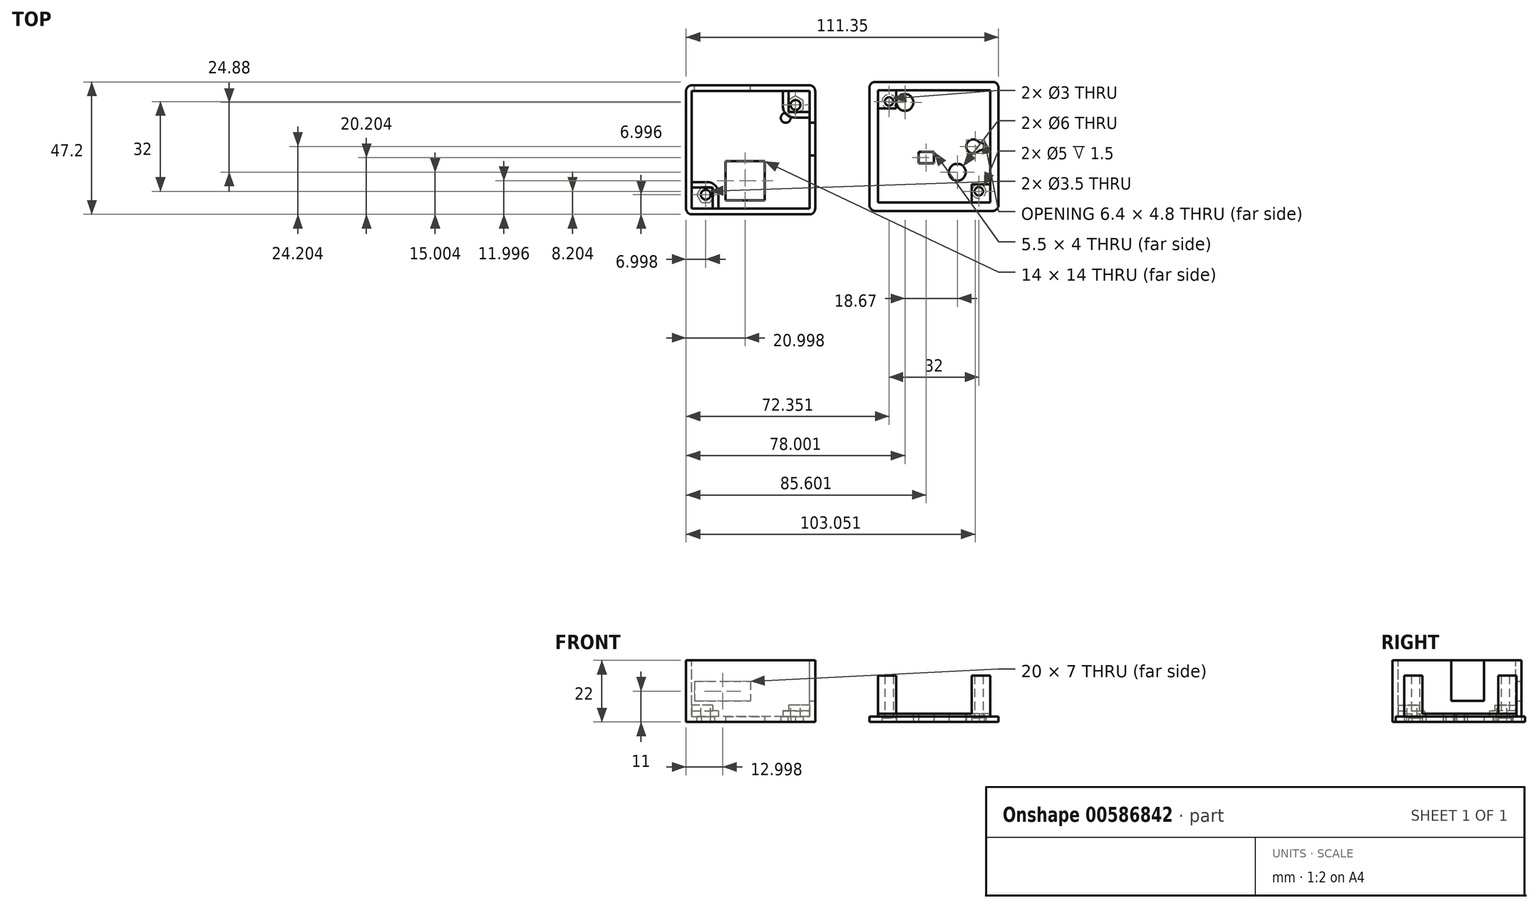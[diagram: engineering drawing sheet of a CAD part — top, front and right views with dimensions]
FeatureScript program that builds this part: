
annotation { "Feature Type Name" : "Feature", "Feature Type Description" : "" }
export const myFeature = defineFeature(function(context is Context, id is Id, definition is map)
    precondition{}
    {
        {
            var Q0;
            Q0=qCreatedBy(makeId("Top.planeOp"),FACE);
            var sketch = newSketch(context, id + "F0", { "sketchPlane" : qUnion([Q0])});
            skLineSegment(sketch, "E0.bottom", {"start": v(-57.81, 60.95) * mm, "end": v(-11.81, 60.95) * mm});
            skLineSegment(sketch, "E0.top", {"start": v(-57.81, 14.95) * mm, "end": v(-11.81, 14.95) * mm});
            skLineSegment(sketch, "E0.left", {"start": v(-57.81, 60.95) * mm, "end": v(-57.81, 14.95) * mm});
            skLineSegment(sketch, "E0.right", {"start": v(-11.81, 60.95) * mm, "end": v(-11.81, 14.95) * mm});
            skSolve(sketch);
        }
        {
            var Q0;
            Q0=makeQuery(id+"F0.imprint","IMPRINT",FACE,{"disambiguationData":[TD([[makeQuery(id+"F0.imprint","IMPRINT",EDGE,{"derivedFrom":sQuery(id+"F0.wireOp",EDGE,"E0.bottom")}),-1.0]])]});
            extrude(context, id + "F1", {"entities" : qUnion([Q0]), "depth" : 22 * mm, "offsetDistance" : 25 * mm});
        }
        {
            var Q0;
            Q0=makeQuery(id+"F1.opExtrude","CAP_FACE",FACE,{"disambiguationData":[OSD([sQuery(id+"F0.wireOp",EDGE,"E0.bottom"),sQuery(id+"F0.wireOp",EDGE,"E0.top"),sQuery(id+"F0.wireOp",EDGE,"E0.left"),sQuery(id+"F0.wireOp",EDGE,"E0.right")])],"isStart":false});
            var sketch = newSketch(context, id + "F2", { "sketchPlane" : qUnion([Q0])});
            skLineSegment(sketch, "E1.bottom", {"start": v(-13.81, 16.95) * mm, "end": v(-55.81, 16.95) * mm});
            skLineSegment(sketch, "E1.top", {"start": v(-13.81, 58.95) * mm, "end": v(-55.81, 58.95) * mm});
            skLineSegment(sketch, "E1.left", {"start": v(-13.81, 16.95) * mm, "end": v(-13.81, 58.95) * mm});
            skLineSegment(sketch, "E1.right", {"start": v(-55.81, 16.95) * mm, "end": v(-55.81, 58.95) * mm});
            skPoint(sketch, "E1.middle", {"position": v(-34.81, 37.95) * mm});
            skPoint(sketch, "E1.middle.positionSnap0", {"position": v(-57.81, 37.95) * mm});
            skPoint(sketch, "E1.middle.positionSnap1", {"position": v(-34.81, 60.95) * mm});
            skPoint(sketch, "E1.centerSnap0", {"position": v(-57.81, 37.95) * mm});
            skPoint(sketch, "E1.centerSnap1", {"position": v(-34.81, 60.95) * mm});
            skSolve(sketch);
        }
        {
            var Q0;
            Q0=makeQuery(id+"F2.imprint","IMPRINT",FACE,{"disambiguationData":[TD([[makeQuery(id+"F2.imprint","IMPRINT",EDGE,{"derivedFrom":sQuery(id+"F2.wireOp",EDGE,"E1.bottom")}),-1.0]])]});
            extrude(context, id + "F3", {"entities" : qUnion([Q0]), "operationType" : NewBodyOperationType.REMOVE, "oppositeDirection" : true, "depth" : 20 * mm, "offsetDistance" : 25 * mm});
        }
        {
            var Q0;
            Q0=makeQuery(id+"F3.boolean.opBoolean","COPY",FACE,{"derivedFrom":makeQuery(id+"F3.opExtrude","CAP_FACE",FACE,{"disambiguationData":[OSD([sQuery(id+"F2.wireOp",EDGE,"E1.bottom"),sQuery(id+"F2.wireOp",EDGE,"E1.top"),sQuery(id+"F2.wireOp",EDGE,"E1.left"),sQuery(id+"F2.wireOp",EDGE,"E1.right")])],"isStart":false})});
            var sketch = newSketch(context, id + "F4", { "sketchPlane" : qUnion([Q0])});
            skLineSegment(sketch, "E2.bottom", {"start": v(-55.81, 16.95) * mm, "end": v(-48.31, 16.95) * mm});
            skLineSegment(sketch, "E2.top", {"start": v(-55.81, 24.45) * mm, "end": v(-48.31, 24.45) * mm});
            skLineSegment(sketch, "E2.left", {"start": v(-55.81, 16.95) * mm, "end": v(-55.81, 24.45) * mm});
            skLineSegment(sketch, "E2.right", {"start": v(-48.31, 16.95) * mm, "end": v(-48.31, 24.45) * mm});
            skLineSegment(sketch, "E3.bottom", {"start": v(-13.81, 58.95) * mm, "end": v(-21.31, 58.95) * mm});
            skLineSegment(sketch, "E3.top", {"start": v(-13.81, 51.45) * mm, "end": v(-21.31, 51.45) * mm});
            skLineSegment(sketch, "E3.left", {"start": v(-13.81, 58.95) * mm, "end": v(-13.81, 51.45) * mm});
            skLineSegment(sketch, "E3.right", {"start": v(-21.31, 58.95) * mm, "end": v(-21.31, 51.45) * mm});
            skSolve(sketch);
        }
        {
            var Q0;
            Q0 = qSketchRegion(id + "F4", true);
            extrude(context, id + "F5", {"entities" : qUnion([Q0]), "operationType" : NewBodyOperationType.ADD, "depth" : 4 * mm, "offsetDistance" : 25 * mm});
        }
        {
            var Q0;
            Q0=makeQuery(id+"F5.boolean.opBoolean","MERGE",FACE,{"derivedFrom":[makeQuery(id+"F1.opExtrude","CAP_FACE",FACE,{"disambiguationData":[OSD([sQuery(id+"F0.wireOp",EDGE,"E0.bottom"),sQuery(id+"F0.wireOp",EDGE,"E0.top"),sQuery(id+"F0.wireOp",EDGE,"E0.left"),sQuery(id+"F0.wireOp",EDGE,"E0.right")])],"isStart":false}),makeQuery(id+"F5.opExtrude","CAP_FACE",FACE,{"disambiguationData":[OSD([sQuery(id+"F4.wireOp",EDGE,"E2.bottom"),sQuery(id+"F4.wireOp",EDGE,"E2.top"),sQuery(id+"F4.wireOp",EDGE,"E2.left"),sQuery(id+"F4.wireOp",EDGE,"E2.right")])],"isStart":false}),makeQuery(id+"F5.opExtrude","CAP_FACE",FACE,{"disambiguationData":[OSD([sQuery(id+"F4.wireOp",EDGE,"LOzcj4NV-yvEm-kmDy-pfsw-HTMoK0iiiUwV.bottom"),sQuery(id+"F4.wireOp",EDGE,"LOzcj4NV-yvEm-kmDy-pfsw-HTMoK0iiiUwV.top"),sQuery(id+"F4.wireOp",EDGE,"LOzcj4NV-yvEm-kmDy-pfsw-HTMoK0iiiUwV.left"),sQuery(id+"F4.wireOp",EDGE,"LOzcj4NV-yvEm-kmDy-pfsw-HTMoK0iiiUwV.right")])],"isStart":false}),makeQuery(id+"F5.opExtrude","CAP_FACE",FACE,{"disambiguationData":[OSD([sQuery(id+"F4.wireOp",EDGE,"E3.bottom"),sQuery(id+"F4.wireOp",EDGE,"E3.top"),sQuery(id+"F4.wireOp",EDGE,"E3.left"),sQuery(id+"F4.wireOp",EDGE,"E3.right")])],"isStart":false}),makeQuery(id+"F5.opExtrude","CAP_FACE",FACE,{"disambiguationData":[OSD([sQuery(id+"F4.wireOp",EDGE,"QqbcK2UQ-hBf6-F2q0-HRpz-6xSYQiyMGXhG.bottom"),sQuery(id+"F4.wireOp",EDGE,"QqbcK2UQ-hBf6-F2q0-HRpz-6xSYQiyMGXhG.top"),sQuery(id+"F4.wireOp",EDGE,"QqbcK2UQ-hBf6-F2q0-HRpz-6xSYQiyMGXhG.left"),sQuery(id+"F4.wireOp",EDGE,"QqbcK2UQ-hBf6-F2q0-HRpz-6xSYQiyMGXhG.right")])],"isStart":false})]});
            var sketch = newSketch(context, id + "F6", { "sketchPlane" : qUnion([Q0])});
            skCircle(sketch, "E4", {"center": v(-18.81, 53.95) * mm, "radius": 1.75 * mm});
            skCircle(sketch, "E5", {"center": v(-50.81, 21.95) * mm, "radius": 1.75 * mm});
            skSolve(sketch);
        }
        {
            var Q0;
            Q0=makeQuery(id+"F3.boolean.opBoolean","COPY",FACE,{"derivedFrom":makeQuery(id+"F3.opExtrude","CAP_FACE",FACE,{"disambiguationData":[OSD([sQuery(id+"F2.wireOp",EDGE,"E1.bottom"),sQuery(id+"F2.wireOp",EDGE,"E1.top"),sQuery(id+"F2.wireOp",EDGE,"E1.left"),sQuery(id+"F2.wireOp",EDGE,"E1.right")])],"isStart":false})});
            var sketch = newSketch(context, id + "F7", { "sketchPlane" : qUnion([Q0])});
            skLineSegment(sketch, "E6.bottom", {"start": v(-21.31, 58.95) * mm, "end": v(-23.31, 58.95) * mm});
            skLineSegment(sketch, "E6.top", {"start": v(-21.31, 51.45) * mm, "end": v(-23.31, 51.45) * mm});
            skLineSegment(sketch, "E6.left", {"start": v(-21.31, 58.95) * mm, "end": v(-21.31, 51.45) * mm});
            skLineSegment(sketch, "E6.right", {"start": v(-23.31, 58.95) * mm, "end": v(-23.31, 51.45) * mm});
            skLineSegment(sketch, "E7.bottom", {"start": v(-23.31, 51.45) * mm, "end": v(-13.81, 51.45) * mm});
            skLineSegment(sketch, "E7.top", {"start": v(-23.31, 49.45) * mm, "end": v(-13.81, 49.45) * mm});
            skLineSegment(sketch, "E7.left", {"start": v(-23.31, 51.45) * mm, "end": v(-23.31, 49.45) * mm});
            skLineSegment(sketch, "E7.right", {"start": v(-13.81, 51.45) * mm, "end": v(-13.81, 49.45) * mm});
            skLineSegment(sketch, "E8.bottom", {"start": v(-55.81, 24.45) * mm, "end": v(-46.31, 24.45) * mm});
            skLineSegment(sketch, "E8.top", {"start": v(-55.81, 26.45) * mm, "end": v(-46.31, 26.45) * mm});
            skLineSegment(sketch, "E8.left", {"start": v(-55.81, 24.45) * mm, "end": v(-55.81, 26.45) * mm});
            skLineSegment(sketch, "E8.right", {"start": v(-46.31, 24.45) * mm, "end": v(-46.31, 26.45) * mm});
            skLineSegment(sketch, "E9.bottom", {"start": v(-48.31, 16.95) * mm, "end": v(-46.31, 16.95) * mm});
            skLineSegment(sketch, "E9.top", {"start": v(-48.31, 24.45) * mm, "end": v(-46.31, 24.45) * mm});
            skLineSegment(sketch, "E9.left", {"start": v(-48.31, 16.95) * mm, "end": v(-48.31, 24.45) * mm});
            skLineSegment(sketch, "E9.right", {"start": v(-46.31, 16.95) * mm, "end": v(-46.31, 24.45) * mm});
            skSolve(sketch);
        }
        {
            var Q0;
            Q0=makeQuery(id+"F7.imprint","IMPRINT",FACE,{"disambiguationData":[TD([[makeQuery(id+"F7.imprint","IMPRINT",EDGE,{"derivedFrom":sQuery(id+"F7.wireOp",EDGE,"E8.bottom")}),1.0]])]});
            var Q1;
            Q1=makeQuery(id+"F7.imprint","IMPRINT",FACE,{"disambiguationData":[TD([[makeQuery(id+"F7.imprint","IMPRINT",EDGE,{"derivedFrom":sQuery(id+"F7.wireOp",EDGE,"E9.bottom")}),-1.0]])]});
            var Q2;
            Q2=makeQuery(id+"F7.imprint","IMPRINT",FACE,{"disambiguationData":[TD([[makeQuery(id+"F7.imprint","IMPRINT",EDGE,{"derivedFrom":sQuery(id+"F7.wireOp",EDGE,"E6.bottom")}),1.0]])]});
            var Q3;
            Q3=makeQuery(id+"F7.imprint","IMPRINT",FACE,{"disambiguationData":[TD([[makeQuery(id+"F7.imprint","IMPRINT",EDGE,{"derivedFrom":sQuery(id+"F7.wireOp",EDGE,"E7.top")}),1.0]])]});
            extrude(context, id + "F8", {"entities" : qUnion([Q0, Q1, Q2, Q3]), "operationType" : NewBodyOperationType.ADD, "depth" : 2 * mm, "offsetDistance" : 25 * mm});
        }
        {
            var Q0;
            Q0=makeQuery(id+"F1.opExtrude","CAP_FACE",FACE,{"disambiguationData":[OSD([sQuery(id+"F0.wireOp",EDGE,"E0.bottom"),sQuery(id+"F0.wireOp",EDGE,"E0.top"),sQuery(id+"F0.wireOp",EDGE,"E0.left"),sQuery(id+"F0.wireOp",EDGE,"E0.right")])],"isStart":true});
            var sketch = newSketch(context, id + "F9", { "sketchPlane" : qUnion([Q0])});
            skCircle(sketch, "E10.cCircle", {"center": v(-18.81, -53.95) * mm, "radius": 2.75 * mm, "construction": true});
            skLineSegment(sketch, "E10.0", {"start": v(-16.06, -52.36) * mm, "end": v(-16.06, -55.53) * mm});
            skLineSegment(sketch, "E10.1", {"start": v(-16.06, -55.53) * mm, "end": v(-18.81, -57.12) * mm});
            skLineSegment(sketch, "E10.2", {"start": v(-18.81, -57.12) * mm, "end": v(-21.56, -55.53) * mm});
            skLineSegment(sketch, "E10.3", {"start": v(-21.56, -55.53) * mm, "end": v(-21.56, -52.36) * mm});
            skLineSegment(sketch, "E10.4", {"start": v(-21.56, -52.36) * mm, "end": v(-18.81, -50.77) * mm});
            skLineSegment(sketch, "E10.5", {"start": v(-18.81, -50.77) * mm, "end": v(-16.06, -52.36) * mm});
            skPoint(sketch, "E10.0.midPoint", {"position": v(-16.06, -53.95) * mm});
            skCircle(sketch, "E11.cCircle", {"center": v(-50.81, -21.95) * mm, "radius": 2.75 * mm, "construction": true});
            skLineSegment(sketch, "E11.0", {"start": v(-49.22, -19.2) * mm, "end": v(-47.64, -21.95) * mm});
            skLineSegment(sketch, "E11.1", {"start": v(-47.64, -21.95) * mm, "end": v(-49.22, -24.7) * mm});
            skLineSegment(sketch, "E11.2", {"start": v(-49.22, -24.7) * mm, "end": v(-52.4, -24.7) * mm});
            skLineSegment(sketch, "E11.3", {"start": v(-52.4, -24.7) * mm, "end": v(-53.99, -21.95) * mm});
            skLineSegment(sketch, "E11.4", {"start": v(-53.99, -21.95) * mm, "end": v(-52.4, -19.2) * mm});
            skLineSegment(sketch, "E11.5", {"start": v(-52.4, -19.2) * mm, "end": v(-49.22, -19.2) * mm});
            skPoint(sketch, "E11.0.midPoint", {"position": v(-48.43, -20.57) * mm});
            skSolve(sketch);
        }
        {
            var Q0;
            Q0=makeQuery(id+"F9.imprint","IMPRINT",FACE,{"disambiguationData":[TD([[makeQuery(id+"F9.imprint","IMPRINT",EDGE,{"derivedFrom":sQuery(id+"F9.wireOp",EDGE,"E10.0")}),-1.0]])]});
            var Q1;
            Q1=makeQuery(id+"F9.imprint","IMPRINT",FACE,{"disambiguationData":[TD([[makeQuery(id+"F9.imprint","IMPRINT",EDGE,{"derivedFrom":sQuery(id+"F9.wireOp",EDGE,"E11.0")}),-1.0]])]});
            extrude(context, id + "F10", {"entities" : qUnion([Q0, Q1]), "operationType" : NewBodyOperationType.REMOVE, "oppositeDirection" : true, "depth" : 2 * mm, "offsetDistance" : 25 * mm});
        }
        {
            var Q0;
            Q0=qCreatedBy(makeId("Top.planeOp"),FACE);
            var sketch = newSketch(context, id + "F11", { "sketchPlane" : qUnion([Q0])});
            skLineSegment(sketch, "E12.bottom", {"start": v(7.54, 62.15) * mm, "end": v(53.54, 62.15) * mm});
            skLineSegment(sketch, "E12.top", {"start": v(7.54, 16.15) * mm, "end": v(53.54, 16.15) * mm});
            skLineSegment(sketch, "E12.left", {"start": v(7.54, 62.15) * mm, "end": v(7.54, 16.15) * mm});
            skLineSegment(sketch, "E12.right", {"start": v(53.54, 62.15) * mm, "end": v(53.54, 16.15) * mm});
            skSolve(sketch);
        }
        {
            var Q0;
            Q0=makeQuery(id+"F11.imprint","IMPRINT",FACE,{"disambiguationData":[TD([[makeQuery(id+"F11.imprint","IMPRINT",EDGE,{"derivedFrom":sQuery(id+"F11.wireOp",EDGE,"E12.bottom")}),-1.0]])]});
            extrude(context, id + "F12", {"entities" : qUnion([Q0]), "depth" : 2 * mm, "offsetDistance" : 25 * mm});
        }
        {
            var Q0;
            Q0=makeQuery(id+"F12.opExtrude","CAP_FACE",FACE,{"disambiguationData":[OSD([sQuery(id+"F11.wireOp",EDGE,"E12.bottom"),sQuery(id+"F11.wireOp",EDGE,"E12.top"),sQuery(id+"F11.wireOp",EDGE,"E12.left"),sQuery(id+"F11.wireOp",EDGE,"E12.right")])],"isStart":false});
            var sketch = newSketch(context, id + "F13", { "sketchPlane" : qUnion([Q0])});
            skLineSegment(sketch, "E13.bottom", {"start": v(50.54, 19.15) * mm, "end": v(10.54, 19.15) * mm});
            skLineSegment(sketch, "E13.top", {"start": v(50.54, 59.15) * mm, "end": v(10.54, 59.15) * mm});
            skLineSegment(sketch, "E13.left", {"start": v(50.54, 19.15) * mm, "end": v(50.54, 59.15) * mm});
            skLineSegment(sketch, "E13.right", {"start": v(10.54, 19.15) * mm, "end": v(10.54, 59.15) * mm});
            skPoint(sketch, "E13.middle", {"position": v(30.54, 39.15) * mm});
            skPoint(sketch, "E13.middle.positionSnap0", {"position": v(7.54, 39.15) * mm});
            skPoint(sketch, "E13.middle.positionSnap1", {"position": v(30.54, 62.15) * mm});
            skPoint(sketch, "E13.centerSnap0", {"position": v(7.54, 39.15) * mm});
            skPoint(sketch, "E13.centerSnap1", {"position": v(30.54, 62.15) * mm});
            skSolve(sketch);
        }
        {
            var Q0;
            Q0=makeQuery(id+"F13.imprint","IMPRINT",FACE,{"disambiguationData":[TD([[makeQuery(id+"F13.imprint","IMPRINT",EDGE,{"derivedFrom":sQuery(id+"F13.wireOp",EDGE,"E13.bottom")}),-1.0]])]});
            extrude(context, id + "F14", {"entities" : qUnion([Q0]), "operationType" : NewBodyOperationType.ADD, "depth" : 1 * mm, "offsetDistance" : 25 * mm});
        }
        {
            var Q0;
            Q0=makeQuery(id+"F14.opExtrude","CAP_FACE",FACE,{"disambiguationData":[OSD([sQuery(id+"F13.wireOp",EDGE,"E13.bottom"),sQuery(id+"F13.wireOp",EDGE,"E13.top"),sQuery(id+"F13.wireOp",EDGE,"E13.left"),sQuery(id+"F13.wireOp",EDGE,"E13.right")])],"isStart":false});
            var sketch = newSketch(context, id + "F15", { "sketchPlane" : qUnion([Q0])});
            skLineSegment(sketch, "E14.bottom", {"start": v(10.54, 59.15) * mm, "end": v(17.04, 59.15) * mm});
            skLineSegment(sketch, "E14.top", {"start": v(10.54, 52.65) * mm, "end": v(17.04, 52.65) * mm});
            skLineSegment(sketch, "E14.left", {"start": v(10.54, 59.15) * mm, "end": v(10.54, 52.65) * mm});
            skLineSegment(sketch, "E14.right", {"start": v(17.04, 59.15) * mm, "end": v(17.04, 52.65) * mm});
            skLineSegment(sketch, "E15.bottom", {"start": v(10.54, 19.15) * mm, "end": v(17.04, 19.15) * mm});
            skLineSegment(sketch, "E15.top", {"start": v(10.54, 25.65) * mm, "end": v(17.04, 25.65) * mm});
            skLineSegment(sketch, "E15.left", {"start": v(10.54, 19.15) * mm, "end": v(10.54, 25.65) * mm});
            skLineSegment(sketch, "E15.right", {"start": v(17.04, 19.15) * mm, "end": v(17.04, 25.65) * mm});
            skLineSegment(sketch, "E16.bottom", {"start": v(50.54, 19.15) * mm, "end": v(44.04, 19.15) * mm});
            skLineSegment(sketch, "E16.top", {"start": v(50.54, 25.65) * mm, "end": v(44.04, 25.65) * mm});
            skLineSegment(sketch, "E16.left", {"start": v(50.54, 19.15) * mm, "end": v(50.54, 25.65) * mm});
            skLineSegment(sketch, "E16.right", {"start": v(44.04, 19.15) * mm, "end": v(44.04, 25.65) * mm});
            skLineSegment(sketch, "E17.bottom", {"start": v(50.54, 59.15) * mm, "end": v(44.04, 59.15) * mm});
            skLineSegment(sketch, "E17.top", {"start": v(50.54, 52.65) * mm, "end": v(44.04, 52.65) * mm});
            skLineSegment(sketch, "E17.left", {"start": v(50.54, 59.15) * mm, "end": v(50.54, 52.65) * mm});
            skLineSegment(sketch, "E17.right", {"start": v(44.04, 59.15) * mm, "end": v(44.04, 52.65) * mm});
            skSolve(sketch);
        }
        {
            var Q0;
            Q0=makeQuery(id+"F15.imprint","IMPRINT",FACE,{"disambiguationData":[TD([[makeQuery(id+"F15.imprint","IMPRINT",EDGE,{"derivedFrom":sQuery(id+"F15.wireOp",EDGE,"E14.bottom")}),1.0]])]});
            var Q1;
            Q1=makeQuery(id+"F15.imprint","IMPRINT",FACE,{"disambiguationData":[TD([[makeQuery(id+"F15.imprint","IMPRINT",EDGE,{"derivedFrom":sQuery(id+"F15.wireOp",EDGE,"E16.bottom")}),-1.0]])]});
            extrude(context, id + "F16", {"entities" : qUnion([Q0, Q1]), "operationType" : NewBodyOperationType.ADD, "depth" : 13.5 * mm, "offsetDistance" : 25 * mm});
        }
        {
            var Q0;
            {var subQ6=sQuery(id+"F15.wireOp",EDGE,"E14.top");Q0=makeQuery(id+"F15.imprint","IMPRINT",FACE,{"disambiguationData":[TD([[makeQuery(id+"F15.imprint","IMPRINT",EDGE,{"derivedFrom":subQ6}),-1.0]])]});}
            var sketch = newSketch(context, id + "F17", { "sketchPlane" : qUnion([Q0])});
            skCircle(sketch, "E18", {"center": v(14.54, 55.15) * mm, "radius": 1.5 * mm});
            skCircle(sketch, "E19", {"center": v(46.54, 23.15) * mm, "radius": 1.5 * mm});
            skSolve(sketch);
        }
        {
            var Q0;
            Q0 = qSketchRegion(id + "F17", true);
            extrude(context, id + "F18", {"entities" : qUnion([Q0]), "operationType" : NewBodyOperationType.REMOVE, "depth" : 25 * mm, "offsetDistance" : 25 * mm});
        }
        {
            var Q0;
            Q0 = qSketchRegion(id + "F17", true);
            extrude(context, id + "F19", {"entities" : qUnion([Q0]), "operationType" : NewBodyOperationType.REMOVE, "oppositeDirection" : true, "depth" : 25 * mm, "offsetDistance" : 25 * mm});
        }
        {
            var Q0;
            Q0=makeQuery(id+"F1.opExtrude","SWEPT_FACE",FACE,{"disambiguationData":[OSD([sQuery(id+"F0.wireOp",EDGE,"E0.right")])]});
            var sketch = newSketch(context, id + "F20", { "sketchPlane" : qUnion([Q0])});
            skLineSegment(sketch, "E20.bottom", {"start": v(47.65, 7.5) * mm, "end": v(35.95, 7.5) * mm});
            skLineSegment(sketch, "E20.top", {"start": v(47.65, 22) * mm, "end": v(35.95, 22) * mm});
            skLineSegment(sketch, "E20.left", {"start": v(47.65, 7.5) * mm, "end": v(47.65, 22) * mm});
            skLineSegment(sketch, "E20.right", {"start": v(35.95, 7.5) * mm, "end": v(35.95, 22) * mm});
            skSolve(sketch);
        }
        {
            var Q0;
            Q0=makeQuery(id+"F20.imprint","IMPRINT",FACE,{"disambiguationData":[TD([[makeQuery(id+"F20.imprint","IMPRINT",EDGE,{"derivedFrom":sQuery(id+"F20.wireOp",EDGE,"E20.bottom")}),-1.0]])]});
            extrude(context, id + "F21", {"entities" : qUnion([Q0]), "operationType" : NewBodyOperationType.REMOVE, "oppositeDirection" : true, "depth" : 2 * mm, "offsetDistance" : 25 * mm});
        }
        {
            var Q0;
            Q0=makeQuery(id+"F1.opExtrude","SWEPT_FACE",FACE,{"disambiguationData":[OSD([sQuery(id+"F0.wireOp",EDGE,"E0.bottom")])]});
            var sketch = newSketch(context, id + "F22", { "sketchPlane" : qUnion([Q0])});
            skLineSegment(sketch, "E21.bottom", {"start": v(54.81, 14.5) * mm, "end": v(34.81, 14.5) * mm});
            skLineSegment(sketch, "E21.top", {"start": v(54.81, 7.5) * mm, "end": v(34.81, 7.5) * mm});
            skLineSegment(sketch, "E21.left", {"start": v(54.81, 14.5) * mm, "end": v(54.81, 7.5) * mm});
            skLineSegment(sketch, "E21.right", {"start": v(34.81, 14.5) * mm, "end": v(34.81, 7.5) * mm});
            skSolve(sketch);
        }
        {
            var Q0;
            Q0=makeQuery(id+"F22.imprint","IMPRINT",FACE,{"disambiguationData":[TD([[makeQuery(id+"F22.imprint","IMPRINT",EDGE,{"derivedFrom":sQuery(id+"F22.wireOp",EDGE,"E21.bottom")}),1.0]])]});
            extrude(context, id + "F23", {"entities" : qUnion([Q0]), "operationType" : NewBodyOperationType.REMOVE, "oppositeDirection" : true, "depth" : 2 * mm, "offsetDistance" : 25 * mm});
        }
        {
            var Q0;
            Q0=makeQuery(id+"F12.opExtrude","CAP_FACE",FACE,{"disambiguationData":[OSD([sQuery(id+"F11.wireOp",EDGE,"E12.bottom"),sQuery(id+"F11.wireOp",EDGE,"E12.top"),sQuery(id+"F11.wireOp",EDGE,"E12.left"),sQuery(id+"F11.wireOp",EDGE,"E12.right")])],"isStart":true});
            var sketch = newSketch(context, id + "F24", { "sketchPlane" : qUnion([Q0])});
            skCircle(sketch, "E22", {"center": v(20.2, -54.83) * mm, "radius": 3 * mm});
            skCircle(sketch, "E23", {"center": v(38.86, -29.95) * mm, "radius": 3 * mm});
            skLineSegment(sketch, "E24.bottom", {"start": v(30.54, -33.15) * mm, "end": v(25.04, -33.15) * mm});
            skLineSegment(sketch, "E24.top", {"start": v(30.54, -37.15) * mm, "end": v(25.04, -37.15) * mm});
            skLineSegment(sketch, "E24.left", {"start": v(30.54, -33.15) * mm, "end": v(30.54, -37.15) * mm});
            skLineSegment(sketch, "E24.right", {"start": v(25.04, -33.15) * mm, "end": v(25.04, -37.15) * mm});
            skPoint(sketch, "E25.centerSnap0", {"position": v(53.54, -39.15) * mm});
            skPoint(sketch, "E26.centerSnap0", {"position": v(30.54, -16.15) * mm});
            skCircle(sketch, "E27", {"center": v(44.54, -39.15) * mm, "radius": 2.5 * mm});
            skCircle(sketch, "E28", {"center": v(47.04, -39.15) * mm, "radius": 1.4 * mm});
            skSolve(sketch);
        }
        {
            var Q0;
            Q0=makeQuery(id+"F24.imprint","IMPRINT",FACE,{"disambiguationData":[TD([[makeQuery(id+"F24.imprint","IMPRINT",EDGE,{"derivedFrom":sQuery(id+"F24.wireOp",EDGE,"E23")}),1.0]])]});
            var Q1;
            Q1=makeQuery(id+"F24.imprint","IMPRINT",FACE,{"disambiguationData":[TD([[makeQuery(id+"F24.imprint","IMPRINT",EDGE,{"derivedFrom":sQuery(id+"F24.wireOp",EDGE,"E24.bottom")}),1.0]])]});
            var Q2;
            Q2=makeQuery(id+"F24.imprint","IMPRINT",FACE,{"disambiguationData":[TD([[makeQuery(id+"F24.imprint","IMPRINT",EDGE,{"derivedFrom":sQuery(id+"F24.wireOp",EDGE,"E22")}),1.0]])]});
            var Q3;
            {var subQ0=sQuery(id+"F24.wireOp",EDGE,"JaoblzoS-pej5-TRI1-8fRm-G6TPHiuGWGbo");var subQ1=sQuery(id+"F24.wireOp",EDGE,"E25");var subQ2=makeQuery(id+"F24.imprint","INTERSECT",VERTEX,{"disambiguationData":[OD(0.0)],"derivedFrom":[subQ1,subQ0]});Q3=makeQuery(id+"F24.imprint","IMPRINT",FACE,{"disambiguationData":[TD([[makeQuery(id+"F24.imprint","IMPRINT",EDGE,{"disambiguationData":[TD([[subQ2,-1.0]])],"derivedFrom":subQ1}),1.0]])]});}
            var Q4;
            {var subQ0=sQuery(id+"F24.wireOp",EDGE,"JaoblzoS-pej5-TRI1-8fRm-G6TPHiuGWGbo");var subQ1=sQuery(id+"F24.wireOp",EDGE,"E25");var subQ2=makeQuery(id+"F24.imprint","INTERSECT",VERTEX,{"disambiguationData":[OD(0.0)],"derivedFrom":[subQ1,subQ0]});Q4=makeQuery(id+"F24.imprint","IMPRINT",FACE,{"disambiguationData":[TD([[makeQuery(id+"F24.imprint","IMPRINT",EDGE,{"disambiguationData":[TD([[subQ2,1.0]])],"derivedFrom":subQ1}),-1.0]])]});}
            var Q5;
            {var subQ0=sQuery(id+"F24.wireOp",EDGE,"JaoblzoS-pej5-TRI1-8fRm-G6TPHiuGWGbo");var subQ1=sQuery(id+"F24.wireOp",EDGE,"E25");var subQ2=makeQuery(id+"F24.imprint","INTERSECT",VERTEX,{"disambiguationData":[OD(0.0)],"derivedFrom":[subQ1,subQ0]});Q5=makeQuery(id+"F24.imprint","IMPRINT",FACE,{"disambiguationData":[TD([[makeQuery(id+"F24.imprint","IMPRINT",EDGE,{"disambiguationData":[TD([[subQ2,1.0]])],"derivedFrom":subQ1}),1.0]])]});}
            var Q6;
            {var subQ0=sQuery(id+"F24.wireOp",EDGE,"ce6TCpKv-EX0N-aVAv-0rtV-7w44cOPHWiB4");var subQ1=sQuery(id+"F24.wireOp",EDGE,"E26");var subQ2=makeQuery(id+"F24.imprint","INTERSECT",VERTEX,{"disambiguationData":[OD(0.0)],"derivedFrom":[subQ1,subQ0]});Q6=makeQuery(id+"F24.imprint","IMPRINT",FACE,{"disambiguationData":[TD([[makeQuery(id+"F24.imprint","IMPRINT",EDGE,{"disambiguationData":[TD([[subQ2,-1.0]])],"derivedFrom":subQ1}),1.0]])]});}
            var Q7;
            {var subQ0=sQuery(id+"F24.wireOp",EDGE,"ce6TCpKv-EX0N-aVAv-0rtV-7w44cOPHWiB4");var subQ1=sQuery(id+"F24.wireOp",EDGE,"E26");var subQ2=makeQuery(id+"F24.imprint","INTERSECT",VERTEX,{"disambiguationData":[OD(0.0)],"derivedFrom":[subQ1,subQ0]});Q7=makeQuery(id+"F24.imprint","IMPRINT",FACE,{"disambiguationData":[TD([[makeQuery(id+"F24.imprint","IMPRINT",EDGE,{"disambiguationData":[TD([[subQ2,1.0]])],"derivedFrom":subQ1}),1.0]])]});}
            var Q8;
            {var subQ0=sQuery(id+"F24.wireOp",EDGE,"ce6TCpKv-EX0N-aVAv-0rtV-7w44cOPHWiB4");var subQ1=sQuery(id+"F24.wireOp",EDGE,"E26");var subQ2=makeQuery(id+"F24.imprint","INTERSECT",VERTEX,{"disambiguationData":[OD(0.0)],"derivedFrom":[subQ1,subQ0]});Q8=makeQuery(id+"F24.imprint","IMPRINT",FACE,{"disambiguationData":[TD([[makeQuery(id+"F24.imprint","IMPRINT",EDGE,{"disambiguationData":[TD([[subQ2,1.0]])],"derivedFrom":subQ1}),-1.0]])]});}
            var Q9;
            {var subQ0=sQuery(id+"F24.wireOp",EDGE,"E28");var subQ1=sQuery(id+"F24.wireOp",EDGE,"E27");var subQ2=makeQuery(id+"F24.imprint","INTERSECT",VERTEX,{"disambiguationData":[OD(0.0)],"derivedFrom":[subQ1,subQ0]});Q9=makeQuery(id+"F24.imprint","IMPRINT",FACE,{"disambiguationData":[TD([[makeQuery(id+"F24.imprint","IMPRINT",EDGE,{"disambiguationData":[TD([[subQ2,-1.0]])],"derivedFrom":subQ1}),1.0]])]});}
            var Q10;
            {var subQ0=sQuery(id+"F24.wireOp",EDGE,"E28");var subQ1=sQuery(id+"F24.wireOp",EDGE,"E27");var subQ2=makeQuery(id+"F24.imprint","INTERSECT",VERTEX,{"disambiguationData":[OD(0.0)],"derivedFrom":[subQ1,subQ0]});Q10=makeQuery(id+"F24.imprint","IMPRINT",FACE,{"disambiguationData":[TD([[makeQuery(id+"F24.imprint","IMPRINT",EDGE,{"disambiguationData":[TD([[subQ2,1.0]])],"derivedFrom":subQ1}),-1.0]])]});}
            var Q11;
            {var subQ0=sQuery(id+"F24.wireOp",EDGE,"E28");var subQ1=sQuery(id+"F24.wireOp",EDGE,"E27");var subQ2=makeQuery(id+"F24.imprint","INTERSECT",VERTEX,{"disambiguationData":[OD(0.0)],"derivedFrom":[subQ1,subQ0]});Q11=makeQuery(id+"F24.imprint","IMPRINT",FACE,{"disambiguationData":[TD([[makeQuery(id+"F24.imprint","IMPRINT",EDGE,{"disambiguationData":[TD([[subQ2,1.0]])],"derivedFrom":subQ1}),1.0]])]});}
            extrude(context, id + "F25", {"entities" : qUnion([Q0, Q1, Q2, Q3, Q4, Q5, Q6, Q7, Q8, Q9, Q10, Q11]), "operationType" : NewBodyOperationType.REMOVE, "oppositeDirection" : true, "depth" : 3 * mm, "offsetDistance" : 25 * mm});
        }
        {
            var Q0;
            Q0=makeQuery(id+"F1.opExtrude","CAP_FACE",FACE,{"disambiguationData":[OSD([sQuery(id+"F0.wireOp",EDGE,"E0.bottom"),sQuery(id+"F0.wireOp",EDGE,"E0.top"),sQuery(id+"F0.wireOp",EDGE,"E0.left"),sQuery(id+"F0.wireOp",EDGE,"E0.right")])],"isStart":true});
            var sketch = newSketch(context, id + "F26", { "sketchPlane" : qUnion([Q0])});
            skLineSegment(sketch, "E29.bottom", {"start": v(-43.81, -33.95) * mm, "end": v(-29.81, -33.95) * mm});
            skLineSegment(sketch, "E29.top", {"start": v(-43.81, -19.95) * mm, "end": v(-29.81, -19.95) * mm});
            skLineSegment(sketch, "E29.left", {"start": v(-43.81, -33.95) * mm, "end": v(-43.81, -19.95) * mm});
            skLineSegment(sketch, "E29.right", {"start": v(-29.81, -33.95) * mm, "end": v(-29.81, -19.95) * mm});
            skCircle(sketch, "E30", {"center": v(-22.3, -49.3) * mm, "radius": 1.75 * mm});
            skSolve(sketch);
        }
        {
            var Q0;
            Q0=makeQuery(id+"F12.opExtrude","CAP_FACE",FACE,{"disambiguationData":[OSD([sQuery(id+"F11.wireOp",EDGE,"E12.bottom"),sQuery(id+"F11.wireOp",EDGE,"E12.top"),sQuery(id+"F11.wireOp",EDGE,"E12.left"),sQuery(id+"F11.wireOp",EDGE,"E12.right")])],"isStart":true});
            var sketch = newSketch(context, id + "F27", { "sketchPlane" : qUnion([Q0])});
            skCircle(sketch, "E31", {"center": v(14.54, -55.15) * mm, "radius": 2.5 * mm});
            skCircle(sketch, "E32", {"center": v(46.54, -23.15) * mm, "radius": 2.5 * mm});
            skSolve(sketch);
        }
        {
            var Q0;
            Q0 = qSketchRegion(id + "F26", true);
            extrude(context, id + "F28", {"entities" : qUnion([Q0]), "operationType" : NewBodyOperationType.REMOVE, "oppositeDirection" : true, "depth" : 2 * mm, "offsetDistance" : 25 * mm});
        }
        {
            var Q0;
            Q0=makeQuery(id+"F27.imprint","IMPRINT",FACE,{"disambiguationData":[TD([[makeQuery(id+"F27.imprint","IMPRINT",EDGE,{"derivedFrom":sQuery(id+"F27.wireOp",EDGE,"E31")}),1.0]])]});
            var Q1;
            Q1=makeQuery(id+"F27.imprint","IMPRINT",FACE,{"disambiguationData":[TD([[makeQuery(id+"F27.imprint","IMPRINT",EDGE,{"derivedFrom":sQuery(id+"F27.wireOp",EDGE,"E32")}),1.0]])]});
            extrude(context, id + "F29", {"entities" : qUnion([Q0, Q1]), "operationType" : NewBodyOperationType.REMOVE, "oppositeDirection" : true, "depth" : 1.5 * mm, "offsetDistance" : 25 * mm});
        }
        {
            var Q0;
            Q0 = qSketchRegion(id + "F6", true);
            extrude(context, id + "F30", {"entities" : qUnion([Q0]), "operationType" : NewBodyOperationType.REMOVE, "oppositeDirection" : true, "depth" : 25 * mm, "offsetDistance" : 25 * mm});
        }
        {
            var Q0;
            Q0=makeQuery(id+"F8.opExtrude","SWEPT_EDGE",EDGE,{"disambiguationData":[OSD([sQuery(id+"F7.wireOp",EDGE,"E8.top"),sQuery(id+"F7.wireOp",EDGE,"E8.right")])]});
            var Q1;
            Q1=makeQuery(id+"F5.opExtrude","SWEPT_EDGE",EDGE,{"disambiguationData":[OSD([sQuery(id+"F4.wireOp",EDGE,"LOzcj4NV-yvEm-kmDy-pfsw-HTMoK0iiiUwV.top"),sQuery(id+"F4.wireOp",EDGE,"LOzcj4NV-yvEm-kmDy-pfsw-HTMoK0iiiUwV.right")])]});
            var Q2;
            Q2=makeQuery(id+"F5.opExtrude","SWEPT_EDGE",EDGE,{"disambiguationData":[OSD([sQuery(id+"F4.wireOp",EDGE,"QqbcK2UQ-hBf6-F2q0-HRpz-6xSYQiyMGXhG.top"),sQuery(id+"F4.wireOp",EDGE,"QqbcK2UQ-hBf6-F2q0-HRpz-6xSYQiyMGXhG.right")])]});
            var Q3;
            Q3=makeQuery(id+"F8.opExtrude","SWEPT_EDGE",EDGE,{"disambiguationData":[OSD([sQuery(id+"F7.wireOp",EDGE,"E7.top"),sQuery(id+"F7.wireOp",EDGE,"E7.left")])]});
            fillet(context, id + "F31", {"entities" : qUnion([Q0, Q1, Q2, Q3]), "radius" : 4 * mm, "tangentPropagation" : true, "allowEdgeOverflow" : false});
        }
        {
            var Q0;
            Q0=makeQuery(id+"F1.opExtrude","SWEPT_EDGE",EDGE,{"disambiguationData":[OSD([sQuery(id+"F0.wireOp",EDGE,"E0.top"),sQuery(id+"F0.wireOp",EDGE,"E0.left")])]});
            var Q1;
            Q1=makeQuery(id+"F1.opExtrude","SWEPT_EDGE",EDGE,{"disambiguationData":[OSD([sQuery(id+"F0.wireOp",EDGE,"E0.bottom"),sQuery(id+"F0.wireOp",EDGE,"E0.left")])]});
            var Q2;
            Q2=makeQuery(id+"F1.opExtrude","SWEPT_EDGE",EDGE,{"disambiguationData":[OSD([sQuery(id+"F0.wireOp",EDGE,"E0.bottom"),sQuery(id+"F0.wireOp",EDGE,"E0.right")])]});
            var Q3;
            Q3=makeQuery(id+"F1.opExtrude","SWEPT_EDGE",EDGE,{"disambiguationData":[OSD([sQuery(id+"F0.wireOp",EDGE,"E0.top"),sQuery(id+"F0.wireOp",EDGE,"E0.right")])]});
            var Q4;
            Q4=makeQuery(id+"F12.opExtrude","SWEPT_EDGE",EDGE,{"disambiguationData":[OSD([sQuery(id+"F11.wireOp",EDGE,"E12.top"),sQuery(id+"F11.wireOp",EDGE,"E12.left")])]});
            var Q5;
            Q5=makeQuery(id+"F12.opExtrude","SWEPT_EDGE",EDGE,{"disambiguationData":[OSD([sQuery(id+"F11.wireOp",EDGE,"E12.bottom"),sQuery(id+"F11.wireOp",EDGE,"E12.left")])]});
            var Q6;
            Q6=makeQuery(id+"F12.opExtrude","SWEPT_EDGE",EDGE,{"disambiguationData":[OSD([sQuery(id+"F11.wireOp",EDGE,"E12.bottom"),sQuery(id+"F11.wireOp",EDGE,"E12.right")])]});
            var Q7;
            Q7=makeQuery(id+"F12.opExtrude","SWEPT_EDGE",EDGE,{"disambiguationData":[OSD([sQuery(id+"F11.wireOp",EDGE,"E12.top"),sQuery(id+"F11.wireOp",EDGE,"E12.right")])]});
            fillet(context, id + "F32", {"entities" : qUnion([Q0, Q1, Q2, Q3, Q4, Q5, Q6, Q7]), "radius" : 2 * mm, "tangentPropagation" : true, "allowEdgeOverflow" : false});
        }
    });
